# Revit family: Column_Round
name_source: partatom
category: Generic Models
units: mm (PartAtom-declared; Revit-internal decimal feet)

## family parameters
Always vertical = Yes
Can host rebar = No
Classification Number = 23.25.30.11.14.11
Cut with Voids When Loaded = No
Maintain Annotation Orientation = No
Part Type = Normal
Room Calculation Point = No
Round Connector Dimension = Use Diameter
Shared = No
Work Plane-Based = No

## types (3) — shared parameters
Assembly Code = C3010300
Base-Capital Material = ARCAT - Plastic - Glass-Fiber Reinforced - Tan
Column Material = ARCAT - Plastic - Glass-Fiber Reinforced - White
Construction Details = http://www.arcat.com
Default Elevation = 0' - 0"
Finish = <By Category>
Green Building-LEED = http://www.arcat.com
Height = 7' - 0"
Keynote = 06440
Manufacturer = Generic
Manufacturer Fax = (203) 939-2444
Manufacturer Website = http://www.arcat.com
Model = Generic
Product Data = http://www.arcat.com
Product Properties = http://www.arcat.com
Specification = http://www.arcat.com
zero-valued in all types: Expected Lifespan (Years), Maintenance Schedule (Months), Warranty Duration (Years)

## per-type parameters (varying)
| type | Axial Load Capacity | Column Diameter | Description | Radius |
| 10" | 12000.00 lb | 0' - 10" | 10" Round Column | 0' - 5" |
| 8" | 9000.00 lb | 0' - 8" | 8" Round Column | 0' - 4" |
| 6" | 6000.00 lb | 0' - 6" | 6" Round Column | 0' - 3" |

## geometry (parser evidence)
native form markers: Blend x3, Sweep x5
no freeform markers — native parametric forms only
